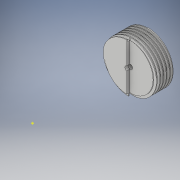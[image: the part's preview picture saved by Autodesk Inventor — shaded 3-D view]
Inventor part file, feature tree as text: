
AUTODESK INVENTOR PART (.ipt)
format: ipt  version: 2018 (Build 220112000, 112)  size: 621,056 bytes
history: native  units: in
note: dims shown in document units (in); Inventor stores cm internally (conversion verified against a paired STEP export)
features: sketch x6, helix x3, extrude x3, other x2, plane x1, loft x1, hole x1, projected_geometry x1
ambient origin geometry x8: Origin, YZ Plane, XZ Plane, XY Plane, X Axis, Y Axis, Z Axis, Center Point
bodies: Solid1 (feature_tree)
feature tree (18):
  sketch  "Sketch1"  dims[d0=2.0in d2=3.9in]
  plane  "Work Plane1"
  loft  "Loft1"
  other  "Work Point1"
  hole  "Hole1"  [1 undecoded]
  other  "Work Axis2"
  sketch  "Sketch6"  dims[d88=1.0in d89=1.0in d11=0.185in d12=0.75in d13=0.375in d14=0.25in d15=0.5635in d16=1.0in d17=0.8108in d41=0.1in]
  helix  "Coil3"  [1 undecoded]
  helix  "Coil4"  [1 undecoded]
  sketch  "Sketch8"  dims[d42=0.1in d43=0.02in]
  extrude  "Extrusion2"  Depth=0.02in
  helix  "Coil5"  [1 undecoded]
  extrude  "Extrusion3"  Depth=1.0in TaperAngle=0.0deg
  extrude  "Extrusion4"  Depth=1.0in
  sketch  "Sketch2"  dims[d3=0.5in d5=0.0in d6=90.0deg d7=0.0in d8=90.0deg]
  projected_geometry  "Projected Loop1"
  sketch  "Sketch9"  dims[d44=0.13in d45=1.0in d46=11.811in d47=-0.0739in d48=90.0deg d49=90.0deg d50=0.0in d51=0.0in]
  sketch  "Sketch11"  dims[d52=0.13in d53=1.0in d54=11.811in d55=0.0756in d56=90.0deg d57=90.0deg d58=0.0in d59=0.0in d61=0.7in d62=0.0in d65=0.13in d66=1.0in d67=2.3622in d68=0.0in d69=90.0deg d70=90.0deg d71=0.0in d72=0.0in d75=3.0in d76=0.0in d78=1.2in d79=1.18in d80=1.2in d81=1.0in d82=0.125in d85=0.18in d86=3.0in d87=0.0in]
note: 4 required parameter values undecoded (feature->parameter linkage not recoverable at this tier; creation-order binding heuristic only, values carry confidence <= 0.55)
